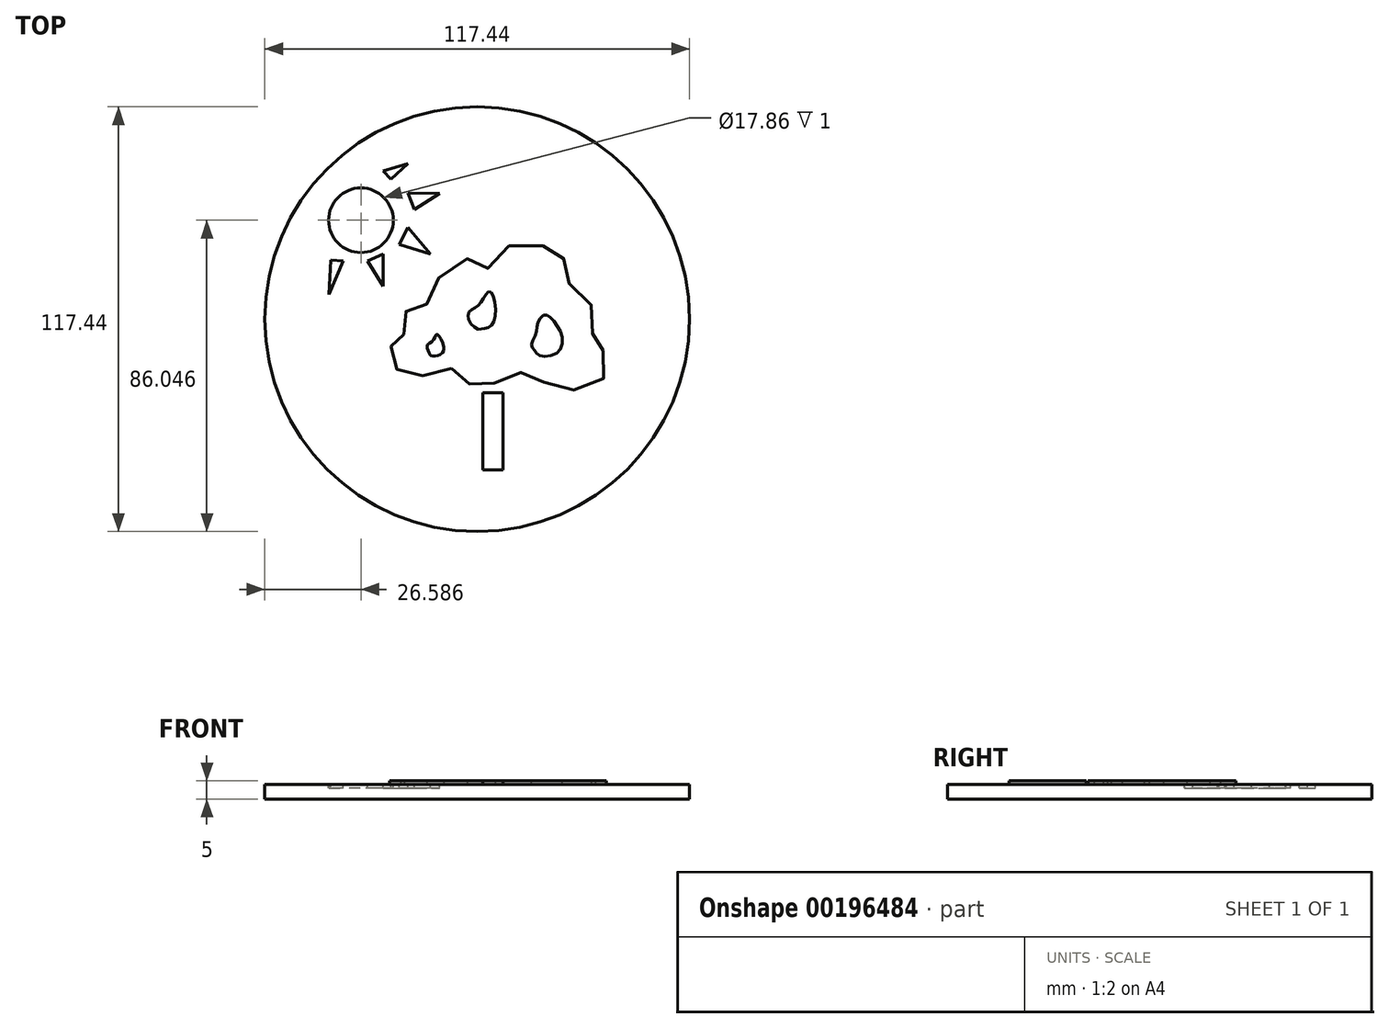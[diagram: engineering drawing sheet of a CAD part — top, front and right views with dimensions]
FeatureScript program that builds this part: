
annotation { "Feature Type Name" : "Feature", "Feature Type Description" : "" }
export const myFeature = defineFeature(function(context is Context, id is Id, definition is map)
    precondition{}
    {
        {
            var Q0;
            Q0=qCreatedBy(makeId("Top.planeOp"),FACE);
            var sketch = newSketch(context, id + "F0", { "sketchPlane" : qUnion([Q0])});
            skCircle(sketch, "E0", {"center": v(0, 0) * mm, "radius": 58.72 * mm});
            skSolve(sketch);
        }
        {
            var Q0;
            Q0 = qSketchRegion(id + "F0", true);
            extrude(context, id + "F1", {"entities" : qUnion([Q0]), "depth" : 4 * mm});
        }
        {
            var Q0;
            Q0=makeQuery(id+"F1.opExtrude","CAP_FACE",FACE,{"disambiguationData":[OSD([sQuery(id+"F0.wireOp",EDGE,"E0")])],"isStart":false});
            var sketch = newSketch(context, id + "F2", { "sketchPlane" : qUnion([Q0])});
            skFitSpline(sketch, "E1", {"points": [v(-7.08, -13.6) * mm, v(-12.37, -15.2) * mm, v(-19.6, -15.2) * mm, v(-22.6, -13.43) * mm, v(-24.2, -9.2) * mm, v(-22.43, -6.02) * mm, v(-20.14, -4.96) * mm, v(-21.02, -2.5) * mm, v(-19.96, 1.74) * mm, v(-17.31, 3.86) * mm, v(-13.43, 4.39) * mm, v(-11.67, 9.5) * mm, v(-4.79, 16.39) * mm, v(0, 15.68) * mm, v(2.8, 13.92) * mm, v(5.8, 18.5) * mm, v(15.68, 20.97) * mm, v(19.91, 19.39) * mm, v(23.62, 17.1) * mm, v(25.03, 13.74) * mm, v(26.1, 8.27) * mm, v(31.74, 3.68) * mm, v(32.44, -1.6) * mm, v(31.91, -7.43) * mm, v(34.91, -8.84) * mm, v(35.44, -14.14) * mm, v(32.8, -19.08) * mm, v(21.68, -18.9) * mm, v(18.33, -17.31) * mm, v(14.27, -14.49) * mm, v(8.62, -16.43) * mm, v(3.86, -17.84) * mm, v(0, -18.2) * mm, v(-5.14, -16.43) * mm, v(-7.08, -13.6) * mm]});
            skSolve(sketch);
        }
        {
            var Q0;
            Q0 = qSketchRegion(id + "F2", true);
            var Q1;
            Q1=makeQuery(id+"F2.imprint","IMPRINT",FACE,{"disambiguationData":[TD([[makeQuery(id+"F2.imprint","IMPRINT",EDGE,{"derivedFrom":sQuery(id+"F2.wireOp",EDGE,"E1")}),-1.0]])]});
            extrude(context, id + "F3", {"entities" : qUnion([Q0, Q1]), "operationType" : NewBodyOperationType.ADD, "depth" : 1 * mm});
        }
        {
            var Q0;
            Q0=makeQuery(id+"F1.opExtrude","CAP_FACE",FACE,{"disambiguationData":[OSD([sQuery(id+"F0.wireOp",EDGE,"E0")])],"isStart":false});
            var sketch = newSketch(context, id + "F4", { "sketchPlane" : qUnion([Q0])});
            skLineSegment(sketch, "E2.bottom", {"start": v(1.57, -20.31) * mm, "end": v(7.21, -20.31) * mm});
            skLineSegment(sketch, "E2.top", {"start": v(1.57, -41.66) * mm, "end": v(7.21, -41.66) * mm});
            skLineSegment(sketch, "E2.left", {"start": v(1.57, -20.31) * mm, "end": v(1.57, -41.66) * mm});
            skLineSegment(sketch, "E2.right", {"start": v(7.21, -20.31) * mm, "end": v(7.21, -41.66) * mm});
            skSolve(sketch);
        }
        {
            var Q0;
            Q0=makeQuery(id+"F4.imprint","IMPRINT",FACE,{"disambiguationData":[TD([[makeQuery(id+"F4.imprint","IMPRINT",EDGE,{"derivedFrom":sQuery(id+"F4.wireOp",EDGE,"E2.bottom")}),-1.0]])]});
            extrude(context, id + "F5", {"entities" : qUnion([Q0]), "operationType" : NewBodyOperationType.ADD, "depth" : 1 * mm});
        }
        {
            var Q0;
            Q0=makeQuery(id+"F1.opExtrude","CAP_FACE",FACE,{"disambiguationData":[OSD([sQuery(id+"F0.wireOp",EDGE,"E0")])],"isStart":false});
            var sketch = newSketch(context, id + "F6", { "sketchPlane" : qUnion([Q0])});
            skCircle(sketch, "E3", {"center": v(-32.13, 27.33) * mm, "radius": 8.93 * mm});
            skSolve(sketch);
        }
        {
            var Q0;
            Q0 = qSketchRegion(id + "F6", true);
            extrude(context, id + "F7", {"entities" : qUnion([Q0]), "operationType" : NewBodyOperationType.REMOVE, "oppositeDirection" : true, "depth" : 1 * mm});
        }
        {
            var Q0;
            Q0=makeQuery(id+"F1.opExtrude","CAP_FACE",FACE,{"disambiguationData":[OSD([sQuery(id+"F0.wireOp",EDGE,"E0")])],"isStart":false});
            var sketch = newSketch(context, id + "F8", { "sketchPlane" : qUnion([Q0])});
            skLineSegment(sketch, "E4", {"start": v(-40.43, 16.39) * mm, "end": v(-40.96, 6.86) * mm});
            skLineSegment(sketch, "E5", {"start": v(-40.96, 6.86) * mm, "end": v(-37.07, 16.03) * mm});
            skLineSegment(sketch, "E6", {"start": v(-37.07, 16.03) * mm, "end": v(-40.43, 16.39) * mm});
            skLineSegment(sketch, "E7", {"start": v(-30.37, 16.03) * mm, "end": v(-25.96, 9.15) * mm});
            skLineSegment(sketch, "E8", {"start": v(-25.96, 9.15) * mm, "end": v(-25.96, 17.97) * mm});
            skLineSegment(sketch, "E9", {"start": v(-25.96, 17.97) * mm, "end": v(-30.37, 16.03) * mm});
            skLineSegment(sketch, "E10", {"start": v(-21.55, 20.62) * mm, "end": v(-12.9, 17.97) * mm});
            skLineSegment(sketch, "E11", {"start": v(-12.9, 17.97) * mm, "end": v(-19.08, 25.39) * mm});
            skLineSegment(sketch, "E12", {"start": v(-19.08, 25.39) * mm, "end": v(-21.55, 20.62) * mm});
            skLineSegment(sketch, "E13", {"start": v(-19.08, 34.91) * mm, "end": v(-17.31, 30.33) * mm});
            skLineSegment(sketch, "E14", {"start": v(-17.31, 30.33) * mm, "end": v(-10.43, 34.74) * mm});
            skLineSegment(sketch, "E15", {"start": v(-10.43, 34.74) * mm, "end": v(-19.08, 34.91) * mm});
            skLineSegment(sketch, "E16", {"start": v(-25.96, 40.91) * mm, "end": v(-23.84, 38.62) * mm});
            skLineSegment(sketch, "E17", {"start": v(-23.84, 38.62) * mm, "end": v(-19.08, 43.02) * mm});
            skLineSegment(sketch, "E18", {"start": v(-25.96, 40.91) * mm, "end": v(-19.08, 43.02) * mm});
            skSolve(sketch);
        }
        {
            var Q0;
            Q0=makeQuery(id+"F8.imprint","IMPRINT",FACE,{"disambiguationData":[TD([[makeQuery(id+"F8.imprint","IMPRINT",EDGE,{"derivedFrom":sQuery(id+"F8.wireOp",EDGE,"E16")}),1.0]])]});
            var Q1;
            Q1=makeQuery(id+"F8.imprint","IMPRINT",FACE,{"disambiguationData":[TD([[makeQuery(id+"F8.imprint","IMPRINT",EDGE,{"derivedFrom":sQuery(id+"F8.wireOp",EDGE,"E13")}),1.0]])]});
            var Q2;
            Q2=makeQuery(id+"F8.imprint","IMPRINT",FACE,{"disambiguationData":[TD([[makeQuery(id+"F8.imprint","IMPRINT",EDGE,{"derivedFrom":sQuery(id+"F8.wireOp",EDGE,"E10")}),1.0]])]});
            var Q3;
            Q3=makeQuery(id+"F8.imprint","IMPRINT",FACE,{"disambiguationData":[TD([[makeQuery(id+"F8.imprint","IMPRINT",EDGE,{"derivedFrom":sQuery(id+"F8.wireOp",EDGE,"E7")}),1.0]])]});
            var Q4;
            Q4=makeQuery(id+"F8.imprint","IMPRINT",FACE,{"disambiguationData":[TD([[makeQuery(id+"F8.imprint","IMPRINT",EDGE,{"derivedFrom":sQuery(id+"F8.wireOp",EDGE,"E4")}),1.0]])]});
            extrude(context, id + "F9", {"entities" : qUnion([Q0, Q1, Q2, Q3, Q4]), "operationType" : NewBodyOperationType.REMOVE, "oppositeDirection" : true, "depth" : 1 * mm});
        }
        {
            var Q0;
            Q0=makeQuery(id+"F3.opExtrude","CAP_FACE",FACE,{"disambiguationData":[OSD([sQuery(id+"F2.wireOp",EDGE,"E1")])],"isStart":false});
            var sketch = newSketch(context, id + "F10", { "sketchPlane" : qUnion([Q0])});
            skFitSpline(sketch, "E19", {"points": [v(17.29, -10.08) * mm, v(15.92, -8.71) * mm, v(15.04, -7.09) * mm, v(16.3, -3.97) * mm, v(16.79, -1.1) * mm, v(18.66, 1.14) * mm, v(20.66, 0) * mm, v(23.4, -4.6) * mm, v(22.15, -9.34) * mm, v(17.29, -10.08) * mm]});
            skFitSpline(sketch, "E20", {"points": [v(3.94, -1.73) * mm, v(1.82, -2.6) * mm, v(0, -2.72) * mm, v(-2.42, 0) * mm, v(-2.05, 2.14) * mm, v(0, 3.51) * mm, v(1.82, 5.76) * mm, v(3.44, 7.63) * mm, v(5.06, 3.51) * mm, v(3.94, -1.73) * mm]});
            skFitSpline(sketch, "E21", {"points": [v(-10.9, -10.08) * mm, v(-12.78, -10.08) * mm, v(-13.4, -9.09) * mm, v(-13.78, -7.21) * mm, v(-12.15, -5.84) * mm, v(-11.16, -4.22) * mm, v(-9.16, -8.21) * mm, v(-10.9, -10.08) * mm]});
            skSolve(sketch);
        }
        {
            var Q0;
            Q0=makeQuery(id+"F10.imprint","IMPRINT",FACE,{"disambiguationData":[TD([[makeQuery(id+"F10.imprint","IMPRINT",EDGE,{"derivedFrom":sQuery(id+"F10.wireOp",EDGE,"E20")}),-1.0]])]});
            var Q1;
            Q1=makeQuery(id+"F10.imprint","IMPRINT",FACE,{"disambiguationData":[TD([[makeQuery(id+"F10.imprint","IMPRINT",EDGE,{"derivedFrom":sQuery(id+"F10.wireOp",EDGE,"E21")}),-1.0]])]});
            var Q2;
            Q2=makeQuery(id+"F10.imprint","IMPRINT",FACE,{"disambiguationData":[TD([[makeQuery(id+"F10.imprint","IMPRINT",EDGE,{"derivedFrom":sQuery(id+"F10.wireOp",EDGE,"E19")}),-1.0]])]});
            extrude(context, id + "F11", {"entities" : qUnion([Q0, Q1, Q2]), "operationType" : NewBodyOperationType.REMOVE, "oppositeDirection" : true, "depth" : 1 * mm});
        }
    });
